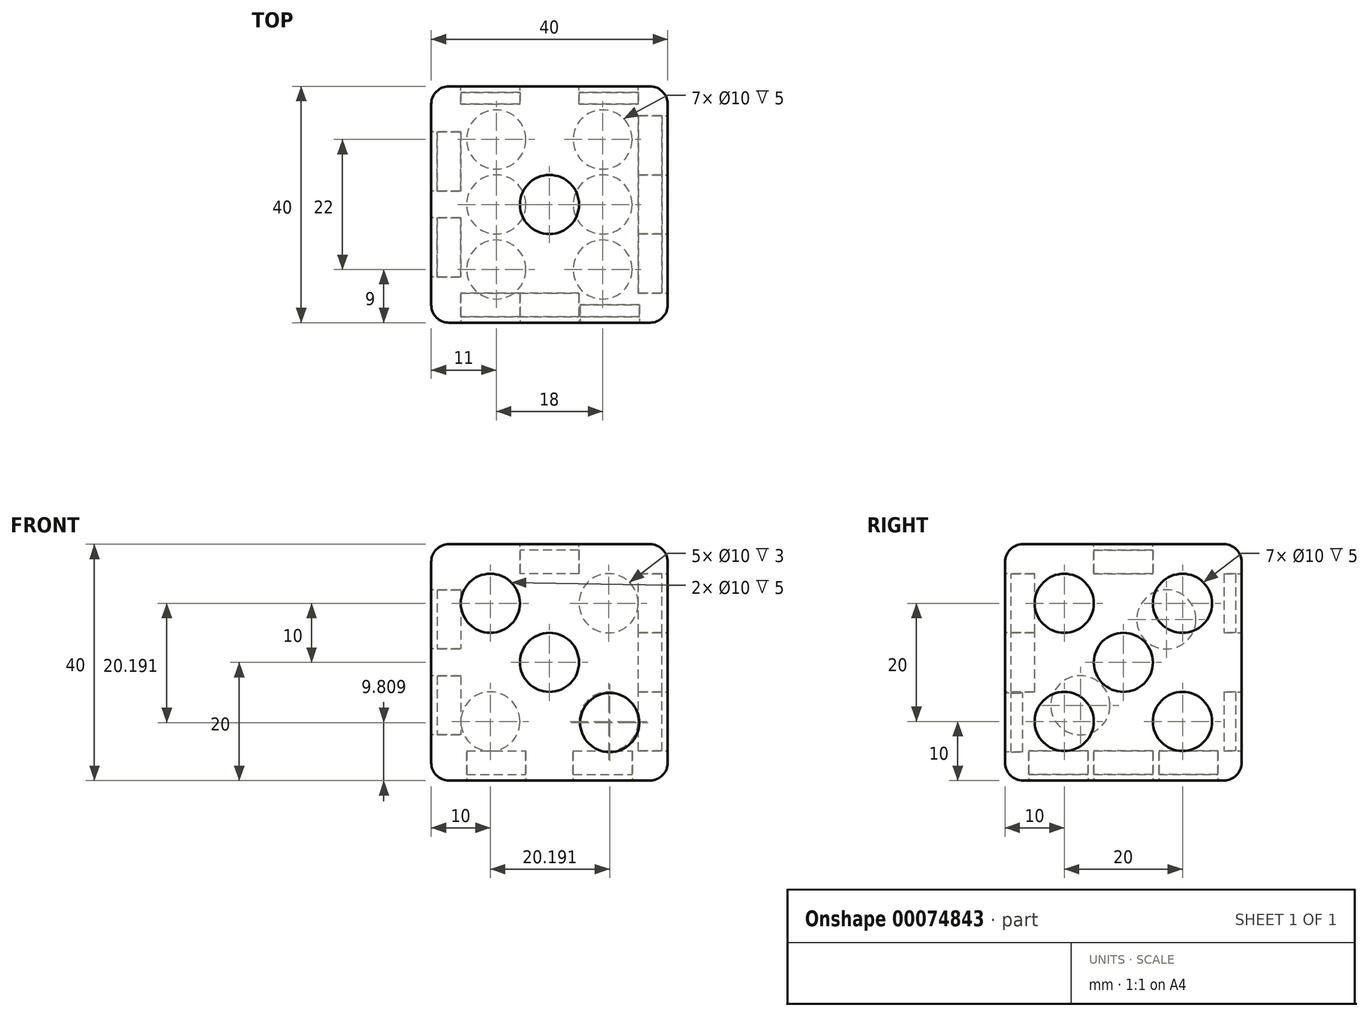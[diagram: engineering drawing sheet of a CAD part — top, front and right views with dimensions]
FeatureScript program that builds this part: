
annotation { "Feature Type Name" : "Feature", "Feature Type Description" : "" }
export const myFeature = defineFeature(function(context is Context, id is Id, definition is map)
    precondition{}
    {
        {
            var Q0;
            Q0=qCreatedBy(makeId("Top.planeOp"),FACE);
            var sketch = newSketch(context, id + "F0", { "sketchPlane" : qUnion([Q0])});
            skLineSegment(sketch, "E0.rect.bottom", {"start": v(20, 20) * mm, "end": v(-20, 20) * mm});
            skLineSegment(sketch, "E0.rect.top", {"start": v(20, -20) * mm, "end": v(-20, -20) * mm});
            skLineSegment(sketch, "E0.rect.left", {"start": v(20, 20) * mm, "end": v(20, -20) * mm});
            skLineSegment(sketch, "E0.rect.right", {"start": v(-20, 20) * mm, "end": v(-20, -20) * mm});
            skPoint(sketch, "E0.rect.middle", {"position": v(0, 0) * mm});
            skSolve(sketch);
        }
        {
            var Q0;
            Q0 = qSketchRegion(id + "F0", true);
            extrude(context, id + "F1", {"entities" : qUnion([Q0]), "depth" : 40 * mm});
        }
        {
            var Q0;
            Q0=makeQuery(id+"F1.opExtrude","CAP_FACE",FACE,{"disambiguationData":[OSD([sQuery(id+"F0.wireOp",EDGE,"E0.rect.bottom"),sQuery(id+"F0.wireOp",EDGE,"E0.rect.top"),sQuery(id+"F0.wireOp",EDGE,"E0.rect.left"),sQuery(id+"F0.wireOp",EDGE,"E0.rect.right")])],"isStart":false});
            var sketch = newSketch(context, id + "F2", { "sketchPlane" : qUnion([Q0])});
            skCircle(sketch, "E1", {"center": v(0, 0) * mm, "radius": 5 * mm});
            skSolve(sketch);
        }
        {
            var Q0;
            Q0 = qSketchRegion(id + "F2", true);
            extrude(context, id + "F3", {"entities" : qUnion([Q0]), "operationType" : NewBodyOperationType.REMOVE, "oppositeDirection" : true, "depth" : 5 * mm});
        }
        {
            var Q0;
            Q0=makeQuery(id+"F1.opExtrude","SWEPT_FACE",FACE,{"disambiguationData":[OSD([sQuery(id+"F0.wireOp",EDGE,"E0.rect.left")])]});
            var sketch = newSketch(context, id + "F4", { "sketchPlane" : qUnion([Q0])});
            skLineSegment(sketch, "E2", {"start": v(0, 40) * mm, "end": v(0, 0) * mm, "construction": true});
            skLineSegment(sketch, "E3", {"start": v(-20, 20) * mm, "end": v(20, 20) * mm, "construction": true});
            skLineSegment(sketch, "E4", {"start": v(-20, 40) * mm, "end": v(20, 0) * mm, "construction": true});
            skLineSegment(sketch, "E5", {"start": v(20, 40) * mm, "end": v(-20, 0) * mm, "construction": true});
            skLineSegment(sketch, "E6", {"start": v(-20, 20) * mm, "end": v(0, 40) * mm, "construction": true});
            skLineSegment(sketch, "E7", {"start": v(20, 20) * mm, "end": v(0, 40) * mm, "construction": true});
            skLineSegment(sketch, "E8", {"start": v(0, 0) * mm, "end": v(-20, 20) * mm, "construction": true});
            skLineSegment(sketch, "E9", {"start": v(0, 0) * mm, "end": v(20, 20) * mm, "construction": true});
            skCircle(sketch, "E10", {"center": v(-10, 30) * mm, "radius": 5 * mm});
            skCircle(sketch, "E11", {"center": v(0, 20) * mm, "radius": 5 * mm});
            skCircle(sketch, "E12", {"center": v(10, 30) * mm, "radius": 5 * mm});
            skCircle(sketch, "E13", {"center": v(10, 10) * mm, "radius": 5 * mm});
            skCircle(sketch, "E14", {"center": v(-10, 10) * mm, "radius": 5 * mm});
            skSolve(sketch);
        }
        {
            var Q0;
            Q0 = qSketchRegion(id + "F4", true);
            extrude(context, id + "F5", {"entities" : qUnion([Q0]), "operationType" : NewBodyOperationType.REMOVE, "oppositeDirection" : true, "depth" : 5 * mm});
        }
        {
            var Q0;
            Q0=makeQuery(id+"F5.boolean.opBoolean","COPY",FACE,{"derivedFrom":makeQuery(id+"F5.opExtrude","CAP_FACE",FACE,{"disambiguationData":[OSD([sQuery(id+"F4.wireOp",EDGE,"E10")])],"isStart":false})});
            var Q1;
            Q1=makeQuery(id+"F5.boolean.opBoolean","COPY",FACE,{"derivedFrom":makeQuery(id+"F5.opExtrude","CAP_FACE",FACE,{"disambiguationData":[OSD([sQuery(id+"F4.wireOp",EDGE,"E12")])],"isStart":false})});
            var Q2;
            Q2=makeQuery(id+"F5.boolean.opBoolean","COPY",FACE,{"derivedFrom":makeQuery(id+"F5.opExtrude","CAP_FACE",FACE,{"disambiguationData":[OSD([sQuery(id+"F4.wireOp",EDGE,"E11")])],"isStart":false})});
            var Q3;
            Q3=makeQuery(id+"F5.boolean.opBoolean","COPY",FACE,{"derivedFrom":makeQuery(id+"F5.opExtrude","CAP_FACE",FACE,{"disambiguationData":[OSD([sQuery(id+"F4.wireOp",EDGE,"E14")])],"isStart":false})});
            var Q4;
            Q4=makeQuery(id+"F5.boolean.opBoolean","COPY",FACE,{"derivedFrom":makeQuery(id+"F5.opExtrude","CAP_FACE",FACE,{"disambiguationData":[OSD([sQuery(id+"F4.wireOp",EDGE,"E13")])],"isStart":false})});
            extrude(context, id + "F6", {"entities" : qUnion([Q0, Q1, Q2, Q3, Q4]), "depth" : 4 * mm});
        }
        {
            var Q0;
            Q0=makeQuery(id+"F3.boolean.opBoolean","COPY",FACE,{"derivedFrom":makeQuery(id+"F3.opExtrude","CAP_FACE",FACE,{"disambiguationData":[OSD([sQuery(id+"F2.wireOp",EDGE,"E1")])],"isStart":false})});
            extrude(context, id + "F7", {"entities" : qUnion([Q0]), "depth" : 4 * mm});
        }
        {
            var Q0;
            Q0=makeQuery(id+"F1.opExtrude","CAP_FACE",FACE,{"disambiguationData":[OSD([sQuery(id+"F0.wireOp",EDGE,"E0.rect.bottom"),sQuery(id+"F0.wireOp",EDGE,"E0.rect.top"),sQuery(id+"F0.wireOp",EDGE,"E0.rect.left"),sQuery(id+"F0.wireOp",EDGE,"E0.rect.right")])],"isStart":true});
            var sketch = newSketch(context, id + "F8", { "sketchPlane" : qUnion([Q0])});
            skCircle(sketch, "E15", {"center": v(-9, 11) * mm, "radius": 5 * mm});
            skCircle(sketch, "E16", {"center": v(-9, 0) * mm, "radius": 5 * mm});
            skCircle(sketch, "E17", {"center": v(-9, -11) * mm, "radius": 5 * mm});
            skCircle(sketch, "E18", {"center": v(9, 11) * mm, "radius": 5 * mm});
            skCircle(sketch, "E19", {"center": v(9, 0) * mm, "radius": 5 * mm});
            skCircle(sketch, "E20", {"center": v(9, -11) * mm, "radius": 5 * mm});
            skLineSegment(sketch, "E21", {"start": v(-9, 20) * mm, "end": v(-9, -20) * mm, "construction": true});
            skLineSegment(sketch, "E22", {"start": v(9, 20) * mm, "end": v(9, -20) * mm, "construction": true});
            skSolve(sketch);
        }
        {
            var Q0;
            Q0=makeQuery(id+"F8.imprint","IMPRINT",FACE,{"disambiguationData":[TD([[makeQuery(id+"F8.imprint","IMPRINT",EDGE,{"derivedFrom":sQuery(id+"F8.wireOp",EDGE,"E15")}),1.0]])]});
            var Q1;
            Q1=makeQuery(id+"F8.imprint","IMPRINT",FACE,{"disambiguationData":[TD([[makeQuery(id+"F8.imprint","IMPRINT",EDGE,{"derivedFrom":sQuery(id+"F8.wireOp",EDGE,"E16")}),1.0]])]});
            var Q2;
            Q2=makeQuery(id+"F8.imprint","IMPRINT",FACE,{"disambiguationData":[TD([[makeQuery(id+"F8.imprint","IMPRINT",EDGE,{"derivedFrom":sQuery(id+"F8.wireOp",EDGE,"E17")}),1.0]])]});
            var Q3;
            Q3=makeQuery(id+"F8.imprint","IMPRINT",FACE,{"disambiguationData":[TD([[makeQuery(id+"F8.imprint","IMPRINT",EDGE,{"derivedFrom":sQuery(id+"F8.wireOp",EDGE,"E20")}),1.0]])]});
            var Q4;
            Q4=makeQuery(id+"F8.imprint","IMPRINT",FACE,{"disambiguationData":[TD([[makeQuery(id+"F8.imprint","IMPRINT",EDGE,{"derivedFrom":sQuery(id+"F8.wireOp",EDGE,"E19")}),1.0]])]});
            var Q5;
            Q5=makeQuery(id+"F8.imprint","IMPRINT",FACE,{"disambiguationData":[TD([[makeQuery(id+"F8.imprint","IMPRINT",EDGE,{"derivedFrom":sQuery(id+"F8.wireOp",EDGE,"E18")}),1.0]])]});
            extrude(context, id + "F9", {"entities" : qUnion([Q0, Q1, Q2, Q3, Q4, Q5]), "operationType" : NewBodyOperationType.REMOVE, "oppositeDirection" : true, "depth" : 5 * mm});
        }
        {
            var Q0;
            Q0=makeQuery(id+"F9.boolean.opBoolean","COPY",FACE,{"derivedFrom":makeQuery(id+"F9.opExtrude","CAP_FACE",FACE,{"disambiguationData":[OSD([sQuery(id+"F8.wireOp",EDGE,"E15")])],"isStart":false})});
            var Q1;
            Q1=makeQuery(id+"F9.boolean.opBoolean","COPY",FACE,{"derivedFrom":makeQuery(id+"F9.opExtrude","CAP_FACE",FACE,{"disambiguationData":[OSD([sQuery(id+"F8.wireOp",EDGE,"E16")])],"isStart":false})});
            var Q2;
            Q2=makeQuery(id+"F9.boolean.opBoolean","COPY",FACE,{"derivedFrom":makeQuery(id+"F9.opExtrude","CAP_FACE",FACE,{"disambiguationData":[OSD([sQuery(id+"F8.wireOp",EDGE,"E17")])],"isStart":false})});
            var Q3;
            Q3=makeQuery(id+"F9.boolean.opBoolean","COPY",FACE,{"derivedFrom":makeQuery(id+"F9.opExtrude","CAP_FACE",FACE,{"disambiguationData":[OSD([sQuery(id+"F8.wireOp",EDGE,"E20")])],"isStart":false})});
            var Q4;
            Q4=makeQuery(id+"F9.boolean.opBoolean","COPY",FACE,{"derivedFrom":makeQuery(id+"F9.opExtrude","CAP_FACE",FACE,{"disambiguationData":[OSD([sQuery(id+"F8.wireOp",EDGE,"E19")])],"isStart":false})});
            var Q5;
            Q5=makeQuery(id+"F9.boolean.opBoolean","COPY",FACE,{"derivedFrom":makeQuery(id+"F9.opExtrude","CAP_FACE",FACE,{"disambiguationData":[OSD([sQuery(id+"F8.wireOp",EDGE,"E18")])],"isStart":false})});
            extrude(context, id + "F10", {"entities" : qUnion([Q0, Q1, Q2, Q3, Q4, Q5]), "depth" : 4 * mm});
        }
        {
            var Q0;
            Q0=makeQuery(id+"F1.opExtrude","SWEPT_FACE",FACE,{"disambiguationData":[OSD([sQuery(id+"F0.wireOp",EDGE,"E0.rect.right")])]});
            var sketch = newSketch(context, id + "F11", { "sketchPlane" : qUnion([Q0])});
            skLineSegment(sketch, "E23", {"start": v(-20, 40) * mm, "end": v(20, 0) * mm, "construction": true});
            skCircle(sketch, "E24", {"center": v(-7.27, 27.27) * mm, "radius": 5 * mm});
            skCircle(sketch, "E25", {"center": v(7.27, 12.73) * mm, "radius": 5 * mm});
            skSolve(sketch);
        }
        {
            var Q0;
            Q0 = qSketchRegion(id + "F11", true);
            var Q1;
            Q1=makeQuery(id+"F11.imprint","IMPRINT",FACE,{"disambiguationData":[TD([[makeQuery(id+"F11.imprint","IMPRINT",EDGE,{"derivedFrom":sQuery(id+"F11.wireOp",EDGE,"E24")}),1.0]])]});
            extrude(context, id + "F12", {"entities" : qUnion([Q0, Q1]), "operationType" : NewBodyOperationType.REMOVE, "oppositeDirection" : true, "depth" : 5 * mm});
        }
        {
            var Q0;
            Q0=makeQuery(id+"F12.boolean.opBoolean","COPY",FACE,{"derivedFrom":makeQuery(id+"F12.opExtrude","CAP_FACE",FACE,{"disambiguationData":[OSD([sQuery(id+"F11.wireOp",EDGE,"E24")])],"isStart":false})});
            var Q1;
            Q1=makeQuery(id+"F12.boolean.opBoolean","COPY",FACE,{"derivedFrom":makeQuery(id+"F12.opExtrude","CAP_FACE",FACE,{"disambiguationData":[OSD([sQuery(id+"F11.wireOp",EDGE,"b031d7a5-4254-4fdf-8dee-6403e7bcc470")])],"isStart":false})});
            var Q2;
            Q2=makeQuery(id+"F12.boolean.opBoolean","COPY",FACE,{"derivedFrom":makeQuery(id+"F12.opExtrude","CAP_FACE",FACE,{"disambiguationData":[OSD([sQuery(id+"F11.wireOp",EDGE,"E25")])],"isStart":false})});
            extrude(context, id + "F13", {"entities" : qUnion([Q0, Q1, Q2]), "depth" : 4 * mm});
        }
        {
            var Q0;
            Q0=makeQuery(id+"F1.opExtrude","SWEPT_FACE",FACE,{"disambiguationData":[OSD([sQuery(id+"F0.wireOp",EDGE,"E0.rect.top")])]});
            var sketch = newSketch(context, id + "F14", { "sketchPlane" : qUnion([Q0])});
            skLineSegment(sketch, "E26", {"start": v(-20, 40) * mm, "end": v(20, 0) * mm, "construction": true});
            skCircle(sketch, "E27", {"center": v(-10, 30) * mm, "radius": 5 * mm});
            skCircle(sketch, "E28", {"center": v(0, 20) * mm, "radius": 5 * mm});
            skCircle(sketch, "E29", {"center": v(10.2, 9.8) * mm, "radius": 5 * mm});
            skSolve(sketch);
        }
        {
            var Q0;
            Q0=makeQuery(id+"F14.imprint","IMPRINT",FACE,{"disambiguationData":[TD([[makeQuery(id+"F14.imprint","IMPRINT",EDGE,{"derivedFrom":sQuery(id+"F14.wireOp",EDGE,"E27")}),1.0]])]});
            var Q1;
            Q1=makeQuery(id+"F14.imprint","IMPRINT",FACE,{"disambiguationData":[TD([[makeQuery(id+"F14.imprint","IMPRINT",EDGE,{"derivedFrom":sQuery(id+"F14.wireOp",EDGE,"E28")}),1.0]])]});
            extrude(context, id + "F15", {"entities" : qUnion([Q0, Q1]), "operationType" : NewBodyOperationType.REMOVE, "oppositeDirection" : true, "depth" : 5 * mm});
        }
        {
            var Q0;
            Q0=makeQuery(id+"F14.imprint","IMPRINT",FACE,{"disambiguationData":[TD([[makeQuery(id+"F14.imprint","IMPRINT",EDGE,{"derivedFrom":sQuery(id+"F14.wireOp",EDGE,"E29")}),1.0]])]});
            extrude(context, id + "F16", {"entities" : qUnion([Q0]), "operationType" : NewBodyOperationType.REMOVE, "oppositeDirection" : true, "depth" : 3 * mm});
        }
        {
            var Q0;
            Q0=makeQuery(id+"F15.boolean.opBoolean","COPY",FACE,{"derivedFrom":makeQuery(id+"F15.opExtrude","CAP_FACE",FACE,{"disambiguationData":[OSD([sQuery(id+"F14.wireOp",EDGE,"E27")])],"isStart":false})});
            var Q1;
            Q1=makeQuery(id+"F15.boolean.opBoolean","COPY",FACE,{"derivedFrom":makeQuery(id+"F15.opExtrude","CAP_FACE",FACE,{"disambiguationData":[OSD([sQuery(id+"F14.wireOp",EDGE,"E28")])],"isStart":false})});
            extrude(context, id + "F17", {"entities" : qUnion([Q0, Q1]), "depth" : 4 * mm});
        }
        {
            var Q0;
            Q0=makeQuery(id+"F16.boolean.opBoolean","COPY",FACE,{"derivedFrom":makeQuery(id+"F16.opExtrude","CAP_FACE",FACE,{"disambiguationData":[OSD([sQuery(id+"F14.wireOp",EDGE,"E29")])],"isStart":false})});
            extrude(context, id + "F18", {"entities" : qUnion([Q0]), "depth" : 2 * mm});
        }
        {
            var Q0;
            Q0=makeQuery(id+"F1.opExtrude","SWEPT_FACE",FACE,{"disambiguationData":[OSD([sQuery(id+"F0.wireOp",EDGE,"E0.rect.bottom")])]});
            var sketch = newSketch(context, id + "F19", { "sketchPlane" : qUnion([Q0])});
            skLineSegment(sketch, "E30", {"start": v(-10, 40) * mm, "end": v(-10, 0) * mm, "construction": true});
            skLineSegment(sketch, "E31", {"start": v(-20, 10) * mm, "end": v(20, 10) * mm, "construction": true});
            skLineSegment(sketch, "E32", {"start": v(10, 0) * mm, "end": v(10, 40) * mm, "construction": true});
            skLineSegment(sketch, "E33", {"start": v(20, 30) * mm, "end": v(-20, 30) * mm, "construction": true});
            skCircle(sketch, "E34", {"center": v(-10, 30) * mm, "radius": 5 * mm});
            skCircle(sketch, "E35", {"center": v(10, 30) * mm, "radius": 5 * mm});
            skCircle(sketch, "E36", {"center": v(10, 10) * mm, "radius": 5 * mm});
            skCircle(sketch, "E37", {"center": v(-10, 10) * mm, "radius": 5 * mm});
            skSolve(sketch);
        }
        {
            var Q0;
            Q0 = qSketchRegion(id + "F19", true);
            extrude(context, id + "F20", {"entities" : qUnion([Q0]), "operationType" : NewBodyOperationType.REMOVE, "oppositeDirection" : true, "depth" : 3 * mm});
        }
        {
            var Q0;
            Q0=makeQuery(id+"F20.boolean.opBoolean","COPY",FACE,{"derivedFrom":makeQuery(id+"F20.opExtrude","CAP_FACE",FACE,{"disambiguationData":[OSD([sQuery(id+"F19.wireOp",EDGE,"E34")])],"isStart":false})});
            var Q1;
            Q1=makeQuery(id+"F20.boolean.opBoolean","COPY",FACE,{"derivedFrom":makeQuery(id+"F20.opExtrude","CAP_FACE",FACE,{"disambiguationData":[OSD([sQuery(id+"F19.wireOp",EDGE,"E35")])],"isStart":false})});
            var Q2;
            Q2=makeQuery(id+"F20.boolean.opBoolean","COPY",FACE,{"derivedFrom":makeQuery(id+"F20.opExtrude","CAP_FACE",FACE,{"disambiguationData":[OSD([sQuery(id+"F19.wireOp",EDGE,"E36")])],"isStart":false})});
            var Q3;
            Q3=makeQuery(id+"F20.boolean.opBoolean","COPY",FACE,{"derivedFrom":makeQuery(id+"F20.opExtrude","CAP_FACE",FACE,{"disambiguationData":[OSD([sQuery(id+"F19.wireOp",EDGE,"E37")])],"isStart":false})});
            extrude(context, id + "F21", {"entities" : qUnion([Q0, Q1, Q2, Q3]), "depth" : 2 * mm});
        }
        {
            var Q0;
            Q0=makeQuery(id+"F1.opExtrude","CAP_EDGE",EDGE,{"disambiguationData":[OSD([sQuery(id+"F0.wireOp",EDGE,"E0.rect.right")])],"isStart":false});
            var Q1;
            Q1=makeQuery(id+"F1.opExtrude","CAP_EDGE",EDGE,{"disambiguationData":[OSD([sQuery(id+"F0.wireOp",EDGE,"E0.rect.bottom")])],"isStart":false});
            var Q2;
            Q2=makeQuery(id+"F1.opExtrude","CAP_EDGE",EDGE,{"disambiguationData":[OSD([sQuery(id+"F0.wireOp",EDGE,"E0.rect.top")])],"isStart":false});
            var Q3;
            Q3=makeQuery(id+"F1.opExtrude","SWEPT_EDGE",EDGE,{"disambiguationData":[OSD([sQuery(id+"F0.wireOp",EDGE,"E0.rect.top"),sQuery(id+"F0.wireOp",EDGE,"E0.rect.right")])]});
            var Q4;
            Q4=makeQuery(id+"F1.opExtrude","CAP_EDGE",EDGE,{"disambiguationData":[OSD([sQuery(id+"F0.wireOp",EDGE,"E0.rect.left")])],"isStart":false});
            var Q5;
            Q5=makeQuery(id+"F1.opExtrude","SWEPT_EDGE",EDGE,{"disambiguationData":[OSD([sQuery(id+"F0.wireOp",EDGE,"E0.rect.top"),sQuery(id+"F0.wireOp",EDGE,"E0.rect.left")])]});
            var Q6;
            Q6=makeQuery(id+"F1.opExtrude","SWEPT_EDGE",EDGE,{"disambiguationData":[OSD([sQuery(id+"F0.wireOp",EDGE,"E0.rect.bottom"),sQuery(id+"F0.wireOp",EDGE,"E0.rect.left")])]});
            var Q7;
            Q7=makeQuery(id+"F1.opExtrude","SWEPT_EDGE",EDGE,{"disambiguationData":[OSD([sQuery(id+"F0.wireOp",EDGE,"E0.rect.bottom"),sQuery(id+"F0.wireOp",EDGE,"E0.rect.right")])]});
            var Q8;
            Q8=makeQuery(id+"F1.opExtrude","CAP_EDGE",EDGE,{"disambiguationData":[OSD([sQuery(id+"F0.wireOp",EDGE,"E0.rect.right")])],"isStart":true});
            var Q9;
            Q9=makeQuery(id+"F1.opExtrude","CAP_EDGE",EDGE,{"disambiguationData":[OSD([sQuery(id+"F0.wireOp",EDGE,"E0.rect.bottom")])],"isStart":true});
            var Q10;
            Q10=makeQuery(id+"F1.opExtrude","CAP_EDGE",EDGE,{"disambiguationData":[OSD([sQuery(id+"F0.wireOp",EDGE,"E0.rect.top")])],"isStart":true});
            var Q11;
            Q11=makeQuery(id+"F1.opExtrude","CAP_EDGE",EDGE,{"disambiguationData":[OSD([sQuery(id+"F0.wireOp",EDGE,"E0.rect.left")])],"isStart":true});
            fillet(context, id + "F22", {"entities" : qUnion([Q0, Q1, Q2, Q3, Q4, Q5, Q6, Q7, Q8, Q9, Q10, Q11]), "radius" : 3 * mm, "tangentPropagation" : true, "allowEdgeOverflow" : false});
        }
    });
